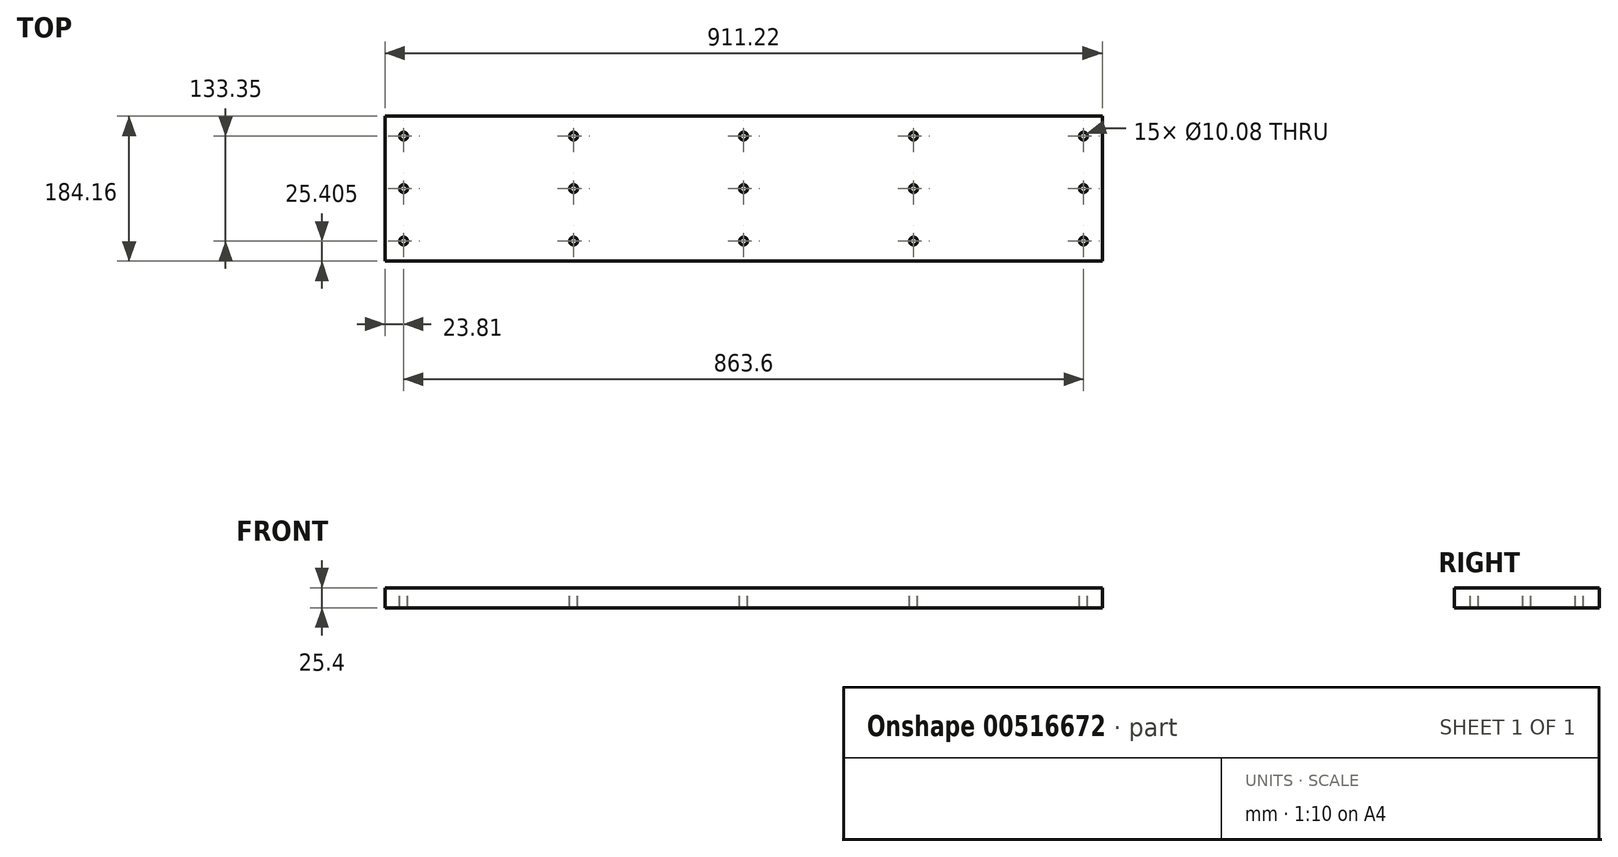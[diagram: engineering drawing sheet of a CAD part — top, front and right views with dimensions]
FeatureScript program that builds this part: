
annotation { "Feature Type Name" : "Feature", "Feature Type Description" : "" }
export const myFeature = defineFeature(function(context is Context, id is Id, definition is map)
    precondition{}
    {
        {
            var Q0;
            Q0=qCreatedBy(makeId("Top.planeOp"),FACE);
            var sketch = newSketch(context, id + "F0", { "sketchPlane" : qUnion([Q0])});
            skLineSegment(sketch, "E0.bottom", {"start": v(455.61, 92.08) * mm, "end": v(-455.61, 92.08) * mm});
            skLineSegment(sketch, "E0.top", {"start": v(455.61, -92.08) * mm, "end": v(-455.61, -92.08) * mm});
            skLineSegment(sketch, "E0.left", {"start": v(455.61, 92.08) * mm, "end": v(455.61, -92.08) * mm});
            skLineSegment(sketch, "E0.right", {"start": v(-455.61, 92.08) * mm, "end": v(-455.61, -92.08) * mm});
            skPoint(sketch, "E1", {"position": v(0, 0) * mm});
            skSolve(sketch);
        }
        {
            var Q0;
            Q0=makeQuery(id+"F0.imprint","IMPRINT",FACE,{"disambiguationData":[TD([[makeQuery(id+"F0.imprint","IMPRINT",EDGE,{"derivedFrom":sQuery(id+"F0.wireOp",EDGE,"E0.bottom")}),1.0]])]});
            extrude(context, id + "F1", {"entities" : qUnion([Q0]), "endBound" : BoundingType.SYMMETRIC, "depth" : 25.4 * mm, "offsetDistance" : 25.4 * mm});
        }
        {
            var Q0;
            Q0=makeQuery(id+"F1.opExtrude","CAP_FACE",FACE,{"disambiguationData":[OSD([sQuery(id+"F0.wireOp",EDGE,"E0.bottom"),sQuery(id+"F0.wireOp",EDGE,"E0.top"),sQuery(id+"F0.wireOp",EDGE,"E0.left"),sQuery(id+"F0.wireOp",EDGE,"E0.right")])],"isStart":false});
            var sketch = newSketch(context, id + "F2", { "sketchPlane" : qUnion([Q0])});
            skPoint(sketch, "E2", {"position": v(-431.8, 66.67) * mm});
            skPoint(sketch, "E3", {"position": v(-431.8, 0) * mm});
            skPoint(sketch, "E4", {"position": v(-431.8, -66.68) * mm});
            skPoint(sketch, "E5", {"position": v(-215.9, -66.68) * mm});
            skPoint(sketch, "E6", {"position": v(-215.9, 0) * mm});
            skPoint(sketch, "E7", {"position": v(-215.9, 66.67) * mm});
            skPoint(sketch, "E8", {"position": v(0, 66.67) * mm});
            skPoint(sketch, "E9", {"position": v(0, 0) * mm});
            skPoint(sketch, "E10", {"position": v(0, -66.68) * mm});
            skPoint(sketch, "E11", {"position": v(215.9, -66.68) * mm});
            skPoint(sketch, "E12", {"position": v(215.9, 0) * mm});
            skPoint(sketch, "E13", {"position": v(215.9, 66.68) * mm});
            skPoint(sketch, "E14", {"position": v(431.8, 66.68) * mm});
            skPoint(sketch, "E15", {"position": v(431.8, 0) * mm});
            skPoint(sketch, "E16", {"position": v(431.8, -66.68) * mm});
            skSolve(sketch);
        }
        {
            var Q0;
            Q0=sQuery(id+"F2.wireOp",VERTEX,"E2");
            var Q1;
            Q1=sQuery(id+"F2.wireOp",VERTEX,"E3");
            var Q2;
            Q2=sQuery(id+"F2.wireOp",VERTEX,"E4");
            var Q3;
            Q3=sQuery(id+"F2.wireOp",VERTEX,"E5");
            var Q4;
            Q4=sQuery(id+"F2.wireOp",VERTEX,"E6");
            var Q5;
            Q5=sQuery(id+"F2.wireOp",VERTEX,"E7");
            var Q6;
            Q6=sQuery(id+"F2.wireOp",VERTEX,"E8");
            var Q7;
            Q7=sQuery(id+"F2.wireOp",VERTEX,"E9");
            var Q8;
            Q8=sQuery(id+"F2.wireOp",VERTEX,"E13");
            var Q9;
            Q9=sQuery(id+"F2.wireOp",VERTEX,"E12");
            var Q10;
            Q10=sQuery(id+"F2.wireOp",VERTEX,"E11");
            var Q11;
            Q11=sQuery(id+"F2.wireOp",VERTEX,"E16");
            var Q12;
            Q12=sQuery(id+"F2.wireOp",VERTEX,"E15");
            var Q13;
            Q13=sQuery(id+"F2.wireOp",VERTEX,"E14");
            var Q14;
            Q14=sQuery(id+"F2.wireOp",VERTEX,"E10");
            var Q15;
            Q15=makeQuery(id+"F1.opExtrude","SWEPT_BODY",BODY,{"disambiguationData":[OSD([sQuery(id+"F0.wireOp",EDGE,"E0.bottom"),sQuery(id+"F0.wireOp",EDGE,"E0.top"),sQuery(id+"F0.wireOp",EDGE,"E0.left"),sQuery(id+"F0.wireOp",EDGE,"E0.right")])]});
            hole(context, id + "F3", {"style" : HoleStyle.SIMPLE, "endStyle" : HoleEndStyle.THROUGH, "standardTappedOrClearance" : lookupTablePath({ "standard" : "ANSI", "fit" : "Normal (ASME)", "size" : "3/8", "type" : "Clearance" }), "standardBlindInLast" : lookupTablePath({ "fit" : "Free", "standard" : "ANSI", "size" : "3/8", "type" : "Clearance" }), "holeDiameter" : 10.08 * mm, "isTappedThrough" : true, "tappedDepth" : 12.7 * mm, "tapClearance" : 3, "locations" : qUnion([Q0, Q1, Q2, Q3, Q4, Q5, Q6, Q7, Q8, Q9, Q10, Q11, Q12, Q13, Q14]), "scope" : qUnion([Q15])});
        }
    });
